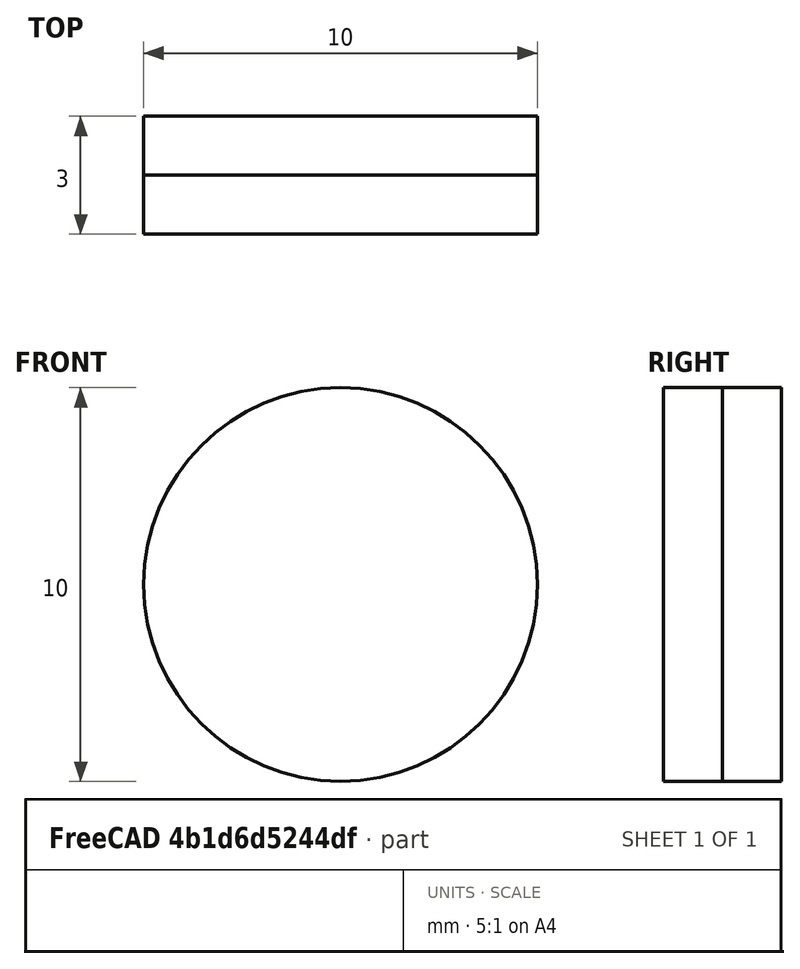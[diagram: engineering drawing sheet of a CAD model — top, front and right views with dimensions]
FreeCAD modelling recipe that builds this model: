
FCSTD DOCUMENT  (FreeCAD 0.22R38467 (Git))
Label: Magnet
License: Public Domain
LicenseURL: https://en.wikipedia.org/wiki/Public_domain
objects: App::Part×3, Part::Cylinder×2, PartDesign::CoordinateSystem×1
note: 3 computed .brp shape members not serialized (recipe doc carries the construction recipe); baked Part::Feature solids carry a one-line shape summary decoded from their .brp

FEATURE [Part::Cylinder] Cylinder  label="SouthMagPole"
  Angle = 360
  AttacherType = Attacher::AttachEngine3D
  FirstAngle = 0
  Height = 1.5
  Placement = pos=(0,0,0) rot=(1,0,0;1.5708rad)
  Radius = 5
  SecondAngle = 0
FEATURE [App::Part] Part001  label="South Pole"
  Group = -> [Cylinder]
  Origin = -> Origin001
FEATURE [Part::Cylinder] Cylinder001  label="NorthMagPole"
  Angle = 360
  AttacherType = Attacher::AttachEngine3D
  FirstAngle = 0
  Height = 1.5
  Placement = pos=(0,-1.5,2e-16) rot=(1,0,0;1.5708rad)
  Radius = 5
  SecondAngle = 0
FEATURE [App::Part] Part002  label="North Pole"
  Group = -> [Cylinder001]
  Origin = -> Origin002
FEATURE [PartDesign::CoordinateSystem] AP  label="Magnet AP"
  AttacherType = Attacher::AttachEngine3D
  AttachmentSupport = -> [Cylinder]
  MapMode = 11
  Placement = pos=(0,0,0) rot=(0.57735,-0.57735,0.57735;2.0944rad)
FEATURE [App::Part] Part  label="Magnet"
  Group = -> [Part001,Part002,AP]
  Origin = -> Origin
  Placement = pos=(-8e-16,-1.5,0) rot=(0,0.707107,-0.707107;3.14159rad)
